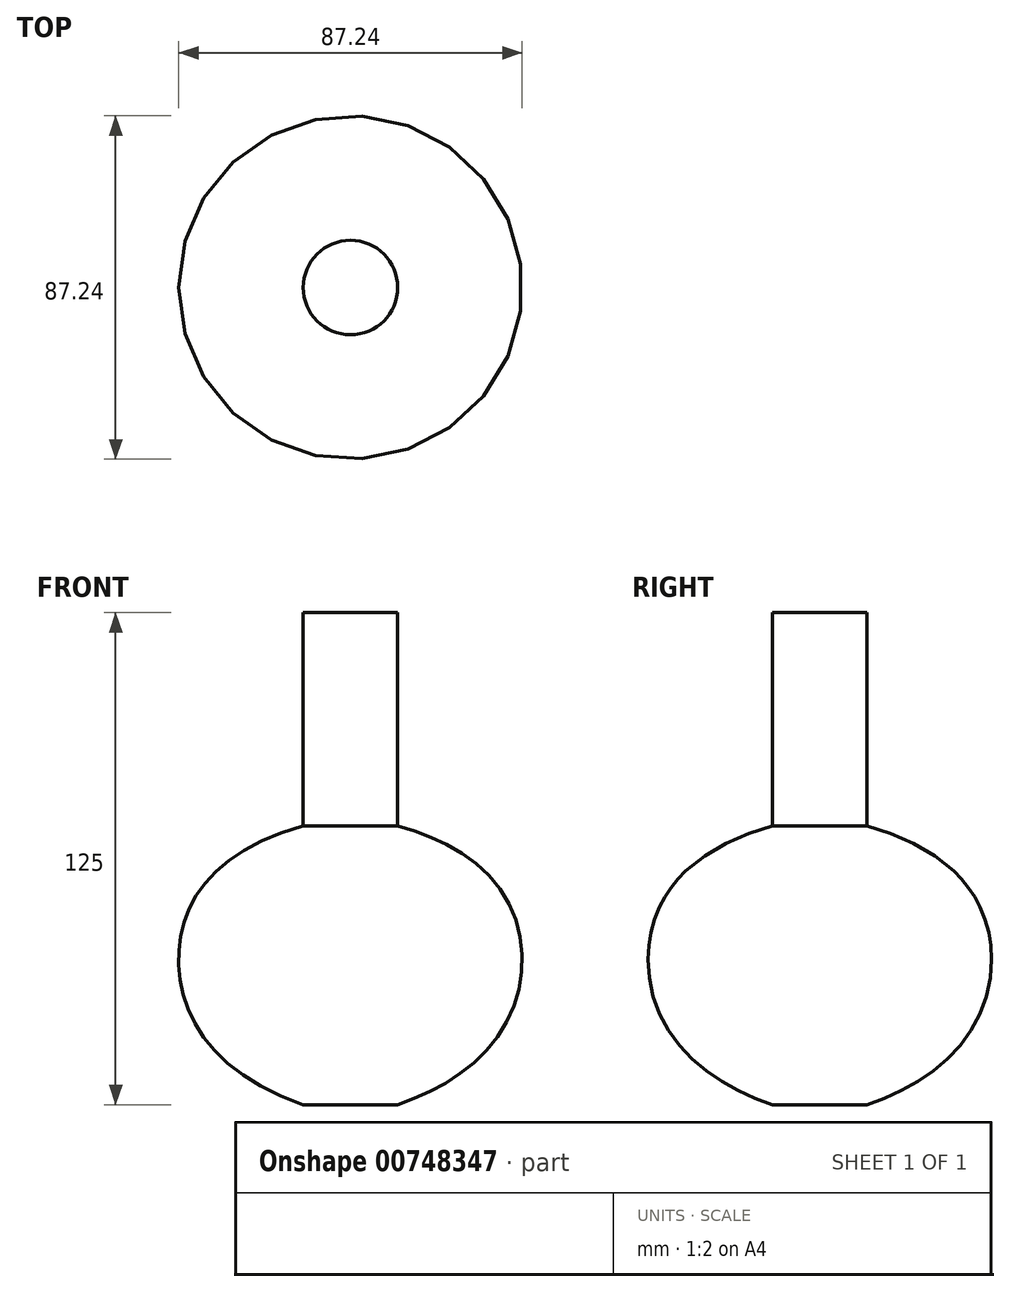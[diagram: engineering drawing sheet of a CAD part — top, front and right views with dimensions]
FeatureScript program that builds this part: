
annotation { "Feature Type Name" : "Feature", "Feature Type Description" : "" }
export const myFeature = defineFeature(function(context is Context, id is Id, definition is map)
    precondition{}
    {
        {
            var Q0;
            Q0=qCreatedBy(makeId("Front.planeOp"),FACE);
            var sketch = newSketch(context, id + "F0", { "sketchPlane" : qUnion([Q0])});
            skLineSegment(sketch, "E0", {"start": v(0, 0) * mm, "end": v(0, 125) * mm});
            skLineSegment(sketch, "E1", {"start": v(0, 125) * mm, "end": v(12, 125) * mm});
            skLineSegment(sketch, "E2", {"start": v(12, 125) * mm, "end": v(12, 70.85) * mm});
            skFitSpline(sketch, "E3", {"points": [v(12, 70.85) * mm, v(43.6, 38.27) * mm, v(12, 0) * mm], "startDerivative": vector(136.78, -38.08) * mm, "endDerivative": vector(-139.9, -47.09) * mm});
            skLineSegment(sketch, "E4", {"start": v(0, 0) * mm, "end": v(12, 0) * mm});
            skSolve(sketch);
        }
        {
            var Q0;
            Q0 = qSketchRegion(id + "F0", true);
            var Q1;
            Q1=sQuery(id+"F0.wireOp",EDGE,"E0");
            revolve(context, id + "F1", {"surfaceOperationType" : NewSurfaceOperationType.NEW, "entities" : qUnion([Q0]), "axis" : qUnion([Q1]), "revolveType" : RevolveType.FULL});
        }
    });
